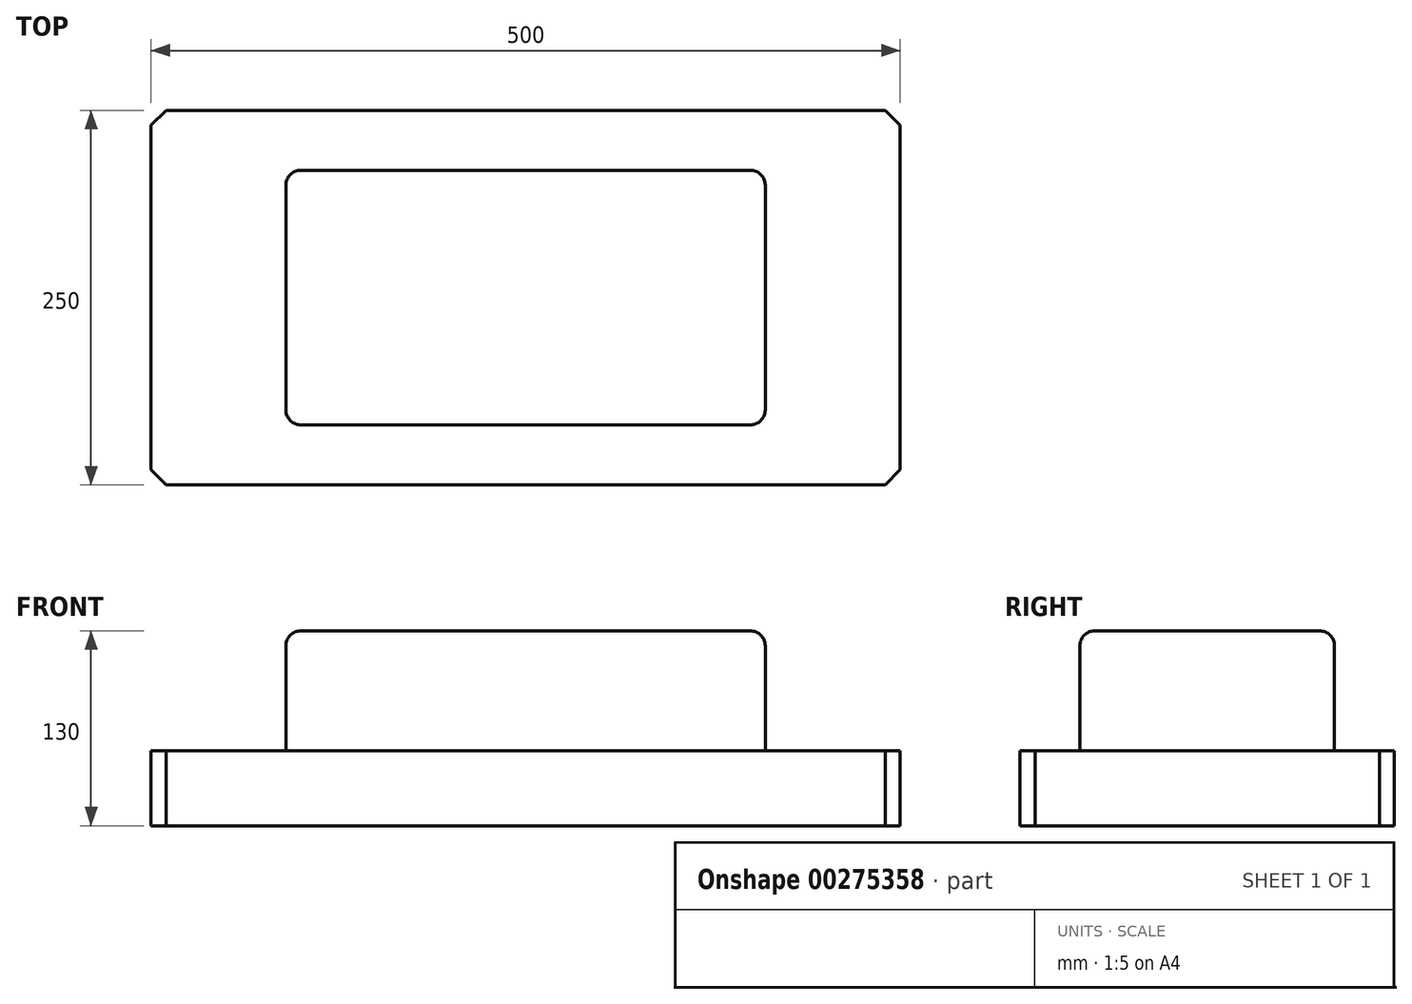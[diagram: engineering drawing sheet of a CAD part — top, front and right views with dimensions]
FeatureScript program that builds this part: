
annotation { "Feature Type Name" : "Feature", "Feature Type Description" : "" }
export const myFeature = defineFeature(function(context is Context, id is Id, definition is map)
    precondition{}
    {
        {
            var Q0;
            Q0=qCreatedBy(makeId("Top.planeOp"),FACE);
            var sketch = newSketch(context, id + "F0", { "sketchPlane" : qUnion([Q0])});
            skLineSegment(sketch, "E0.bottom", {"start": v(-250, -125) * mm, "end": v(250, -125) * mm});
            skLineSegment(sketch, "E0.top", {"start": v(-250, 125) * mm, "end": v(250, 125) * mm});
            skLineSegment(sketch, "E0.left", {"start": v(-250, -125) * mm, "end": v(-250, 125) * mm});
            skLineSegment(sketch, "E0.right", {"start": v(250, -125) * mm, "end": v(250, 125) * mm});
            skPoint(sketch, "E0.middle", {"position": v(0, 0) * mm});
            skSolve(sketch);
        }
        {
            var Q0;
            Q0=makeQuery(id+"F0.imprint","IMPRINT",FACE,{"disambiguationData":[TD([[makeQuery(id+"F0.imprint","IMPRINT",EDGE,{"derivedFrom":sQuery(id+"F0.wireOp",EDGE,"E0.bottom")}),1.0]])]});
            extrude(context, id + "F1", {"entities" : qUnion([Q0]), "endBound" : BoundingType.SYMMETRIC, "depth" : 50 * mm});
        }
        {
            var Q0;
            Q0=makeQuery(id+"F1.opExtrude","CAP_FACE",FACE,{"disambiguationData":[OSD([sQuery(id+"F0.wireOp",EDGE,"E0.bottom"),sQuery(id+"F0.wireOp",EDGE,"E0.top"),sQuery(id+"F0.wireOp",EDGE,"E0.left"),sQuery(id+"F0.wireOp",EDGE,"E0.right")])],"isStart":false});
            var sketch = newSketch(context, id + "F2", { "sketchPlane" : qUnion([Q0])});
            skLineSegment(sketch, "E1.bottom", {"start": v(-160, -85) * mm, "end": v(160, -85) * mm});
            skLineSegment(sketch, "E1.top", {"start": v(-160, 85) * mm, "end": v(160, 85) * mm});
            skLineSegment(sketch, "E1.left", {"start": v(-160, -85) * mm, "end": v(-160, 85) * mm});
            skLineSegment(sketch, "E1.right", {"start": v(160, -85) * mm, "end": v(160, 85) * mm});
            skPoint(sketch, "E1.middle", {"position": v(0, 0) * mm});
            skSolve(sketch);
        }
        {
            var Q0;
            Q0=qSketchRegion(id+"F2",true);
            extrude(context, id + "F3", {"entities" : qUnion([Q0]), "operationType" : NewBodyOperationType.ADD, "depth" : 80 * mm});
        }
        {
            var Q0;
            Q0=makeQuery(id+"F3.opExtrude","CAP_EDGE",EDGE,{"disambiguationData":[OSD([sQuery(id+"F2.wireOp",EDGE,"E1.bottom")])],"isStart":false});
            var Q1;
            Q1=makeQuery(id+"F3.opExtrude","CAP_EDGE",EDGE,{"disambiguationData":[OSD([sQuery(id+"F2.wireOp",EDGE,"E1.right")])],"isStart":false});
            var Q2;
            Q2=makeQuery(id+"F3.opExtrude","CAP_EDGE",EDGE,{"disambiguationData":[OSD([sQuery(id+"F2.wireOp",EDGE,"E1.top")])],"isStart":false});
            var Q3;
            Q3=makeQuery(id+"F3.opExtrude","CAP_EDGE",EDGE,{"disambiguationData":[OSD([sQuery(id+"F2.wireOp",EDGE,"E1.left")])],"isStart":false});
            var Q4;
            Q4=makeQuery(id+"F3.opExtrude","SWEPT_EDGE",EDGE,{"disambiguationData":[OSD([sQuery(id+"F2.wireOp",EDGE,"E1.bottom"),sQuery(id+"F2.wireOp",EDGE,"E1.left")])]});
            var Q5;
            Q5=makeQuery(id+"F3.opExtrude","SWEPT_EDGE",EDGE,{"disambiguationData":[OSD([sQuery(id+"F2.wireOp",EDGE,"E1.bottom"),sQuery(id+"F2.wireOp",EDGE,"E1.right")])]});
            var Q6;
            Q6=makeQuery(id+"F3.opExtrude","SWEPT_EDGE",EDGE,{"disambiguationData":[OSD([sQuery(id+"F2.wireOp",EDGE,"E1.top"),sQuery(id+"F2.wireOp",EDGE,"E1.right")])]});
            var Q7;
            Q7=makeQuery(id+"F3.opExtrude","SWEPT_EDGE",EDGE,{"disambiguationData":[OSD([sQuery(id+"F2.wireOp",EDGE,"E1.top"),sQuery(id+"F2.wireOp",EDGE,"E1.left")])]});
            var Q8;
            Q8=makeQuery(id+"F3.opExtrude","CAP_EDGE",EDGE,{"disambiguationData":[OSD([sQuery(id+"F2.wireOp",EDGE,"E1.left")])],"isStart":true});
            fillet(context, id + "F4", {"entities" : qUnion([Q0, Q1, Q2, Q3, Q4, Q5, Q6, Q7, Q8]), "radius" : 10 * mm, "tangentPropagation" : true, "allowEdgeOverflow" : false});
        }
        {
            var Q0;
            Q0=makeQuery(id+"F1.opExtrude","SWEPT_EDGE",EDGE,{"disambiguationData":[OSD([sQuery(id+"F0.wireOp",EDGE,"E0.bottom"),sQuery(id+"F0.wireOp",EDGE,"E0.left")])]});
            var Q1;
            Q1=makeQuery(id+"F1.opExtrude","SWEPT_EDGE",EDGE,{"disambiguationData":[OSD([sQuery(id+"F0.wireOp",EDGE,"E0.top"),sQuery(id+"F0.wireOp",EDGE,"E0.left")])]});
            var Q2;
            Q2=makeQuery(id+"F1.opExtrude","SWEPT_EDGE",EDGE,{"disambiguationData":[OSD([sQuery(id+"F0.wireOp",EDGE,"E0.top"),sQuery(id+"F0.wireOp",EDGE,"E0.right")])]});
            var Q3;
            Q3=makeQuery(id+"F1.opExtrude","SWEPT_EDGE",EDGE,{"disambiguationData":[OSD([sQuery(id+"F0.wireOp",EDGE,"E0.bottom"),sQuery(id+"F0.wireOp",EDGE,"E0.right")])]});
            chamfer(context, id + "F5", {"entities" : qUnion([Q0, Q1, Q2, Q3]), "width" : 10 * mm, "tangentPropagation" : true});
        }
    });
